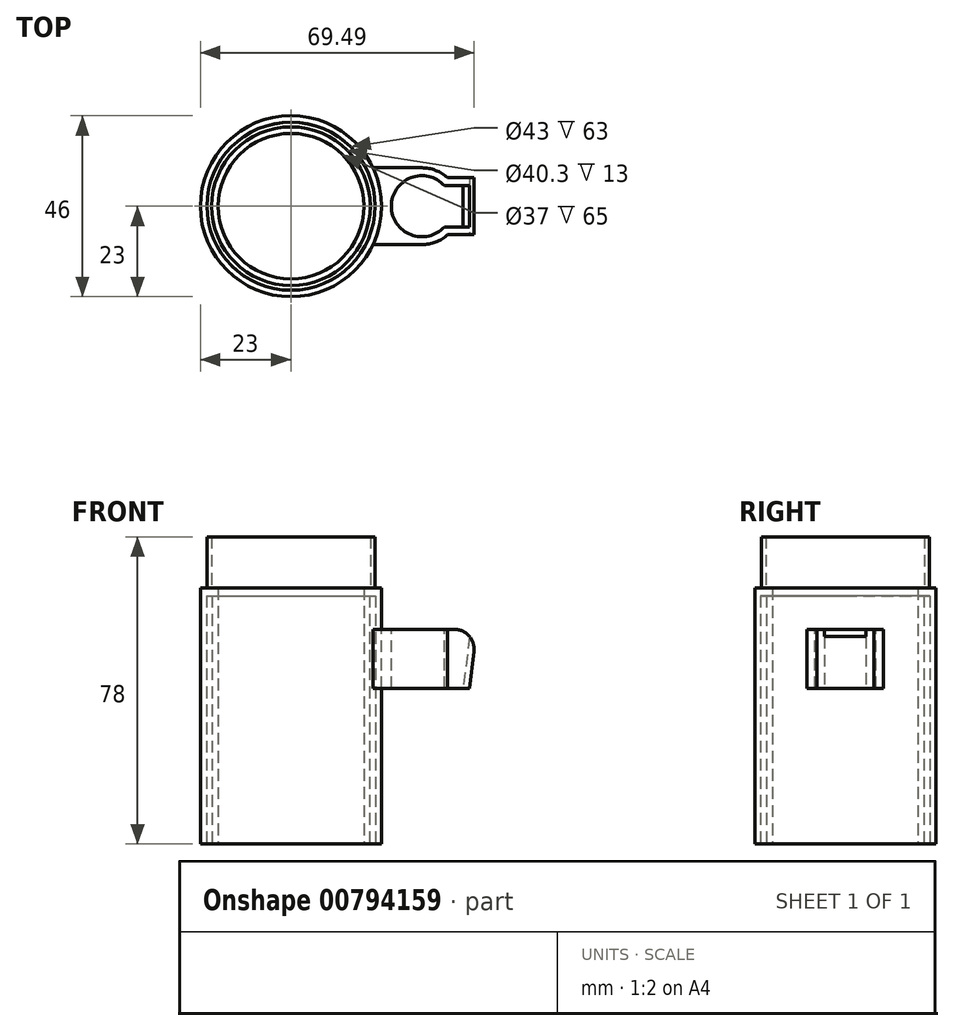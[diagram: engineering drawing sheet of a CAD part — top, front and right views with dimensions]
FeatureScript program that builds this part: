
annotation { "Feature Type Name" : "Feature", "Feature Type Description" : "" }
export const myFeature = defineFeature(function(context is Context, id is Id, definition is map)
    precondition{}
    {
        {
            var Q0;
            Q0=qCreatedBy(makeId("Front.planeOp"),FACE);
            var sketch = newSketch(context, id + "F0", { "sketchPlane" : qUnion([Q0])});
            skLineSegment(sketch, "E0.bottom", {"start": v(0, 0) * mm, "end": v(23, 0) * mm});
            skLineSegment(sketch, "E0.top", {"start": v(0, 65) * mm, "end": v(23, 65) * mm});
            skLineSegment(sketch, "E0.left", {"start": v(0, 0) * mm, "end": v(0, 65) * mm});
            skLineSegment(sketch, "E0.right", {"start": v(23, 0) * mm, "end": v(23, 65) * mm});
            skLineSegment(sketch, "E1.bottom", {"start": v(21.5, 65) * mm, "end": v(23, 65) * mm});
            skLineSegment(sketch, "E1.top", {"start": v(21.5, 0) * mm, "end": v(23, 0) * mm});
            skLineSegment(sketch, "E1.left", {"start": v(21.5, 65) * mm, "end": v(21.5, 0) * mm});
            skLineSegment(sketch, "E1.right", {"start": v(23, 65) * mm, "end": v(23, 0) * mm});
            skLineSegment(sketch, "E2.bottom", {"start": v(20, 65) * mm, "end": v(21.5, 65) * mm});
            skLineSegment(sketch, "E2.top", {"start": v(20, 0) * mm, "end": v(21.5, 0) * mm});
            skLineSegment(sketch, "E2.left", {"start": v(20, 65) * mm, "end": v(20, 0) * mm});
            skLineSegment(sketch, "E3.bottom", {"start": v(20, 65) * mm, "end": v(18.5, 65) * mm});
            skLineSegment(sketch, "E3.top", {"start": v(20, 0) * mm, "end": v(18.5, 0) * mm});
            skLineSegment(sketch, "E3.right", {"start": v(18.5, 65) * mm, "end": v(18.5, 0) * mm});
            skLineSegment(sketch, "E4.bottom", {"start": v(21.35, 65) * mm, "end": v(23, 65) * mm});
            skLineSegment(sketch, "E4.top", {"start": v(21.35, 78) * mm, "end": v(23, 78) * mm});
            skLineSegment(sketch, "E4.left", {"start": v(21.35, 65) * mm, "end": v(21.35, 78) * mm});
            skLineSegment(sketch, "E4.right", {"start": v(23, 65) * mm, "end": v(23, 78) * mm});
            skLineSegment(sketch, "E5.bottom", {"start": v(21.35, 65) * mm, "end": v(20.15, 65) * mm});
            skLineSegment(sketch, "E5.top", {"start": v(21.35, 78) * mm, "end": v(20.15, 78) * mm});
            skLineSegment(sketch, "E5.right", {"start": v(20.15, 65) * mm, "end": v(20.15, 78) * mm});
            skLineSegment(sketch, "E6.bottom", {"start": v(20.15, 78) * mm, "end": v(18.5, 78) * mm});
            skLineSegment(sketch, "E6.top", {"start": v(20.15, 65) * mm, "end": v(18.5, 65) * mm});
            skLineSegment(sketch, "E6.left", {"start": v(20.15, 78) * mm, "end": v(20.15, 65) * mm});
            skLineSegment(sketch, "E6.right", {"start": v(18.5, 78) * mm, "end": v(18.5, 65) * mm});
            skLineSegment(sketch, "E7.bottom", {"start": v(23, 65) * mm, "end": v(0, 65) * mm});
            skLineSegment(sketch, "E7.top", {"start": v(23, 63) * mm, "end": v(0, 63) * mm});
            skLineSegment(sketch, "E7.left", {"start": v(23, 65) * mm, "end": v(23, 63) * mm});
            skLineSegment(sketch, "E7.right", {"start": v(0, 65) * mm, "end": v(0, 63) * mm});
            skSolve(sketch);
        }
        {
            var Q0;
            {var subQ0=sQuery(id+"F0.wireOp",EDGE,"E3.right");var subQ1=sQuery(id+"F0.wireOp",EDGE,"E0.bottom");var subQ2=makeQuery(id+"F0.imprint","INTERSECT",VERTEX,{"derivedFrom":[subQ1,subQ0]});Q0=makeQuery(id+"F0.imprint","IMPRINT",FACE,{"disambiguationData":[TD([[makeQuery(id+"F0.imprint","IMPRINT",EDGE,{"disambiguationData":[TD([[subQ2,-1.0]])],"derivedFrom":subQ1}),1.0]])]});}
            var Q1;
            {var subQ0=sQuery(id+"F0.wireOp",EDGE,"E1.left");var subQ1=sQuery(id+"F0.wireOp",EDGE,"E0.bottom");var subQ2=makeQuery(id+"F0.imprint","INTERSECT",VERTEX,{"derivedFrom":[subQ1,subQ0]});Q1=makeQuery(id+"F0.imprint","IMPRINT",FACE,{"disambiguationData":[TD([[makeQuery(id+"F0.imprint","IMPRINT",EDGE,{"disambiguationData":[TD([[subQ2,-1.0]])],"derivedFrom":subQ1}),1.0]])]});}
            var Q2;
            {var subQ3=sQuery(id+"F0.wireOp",EDGE,"E1.left");var subQ5=sQuery(id+"F0.wireOp",EDGE,"E7.top");var subQ6=makeQuery(id+"F0.imprint","INTERSECT",VERTEX,{"derivedFrom":[subQ3,subQ5]});Q2=makeQuery(id+"F0.imprint","IMPRINT",FACE,{"disambiguationData":[TD([[makeQuery(id+"F0.imprint","IMPRINT",EDGE,{"disambiguationData":[TD([[subQ6,1.0]])],"derivedFrom":subQ3}),1.0]])]});}
            var Q3;
            {var subQ3=sQuery(id+"F0.wireOp",EDGE,"E0.top");var subQ5=makeQuery(id+"F0.imprint","INTERSECT",VERTEX,{"derivedFrom":[subQ3,sQuery(id+"F0.wireOp",EDGE,"E5.right")]});Q3=makeQuery(id+"F0.imprint","IMPRINT",FACE,{"disambiguationData":[TD([[makeQuery(id+"F0.imprint","IMPRINT",EDGE,{"disambiguationData":[TD([[subQ5,-1.0]])],"derivedFrom":subQ3}),-1.0]])]});}
            var Q4;
            {var subQ3=sQuery(id+"F0.wireOp",EDGE,"E2.left");var subQ5=sQuery(id+"F0.wireOp",EDGE,"E7.top");var subQ6=makeQuery(id+"F0.imprint","INTERSECT",VERTEX,{"derivedFrom":[subQ3,subQ5]});Q4=makeQuery(id+"F0.imprint","IMPRINT",FACE,{"disambiguationData":[TD([[makeQuery(id+"F0.imprint","IMPRINT",EDGE,{"disambiguationData":[TD([[subQ6,1.0]])],"derivedFrom":subQ3}),-1.0]])]});}
            var Q5;
            {var subQ2=sQuery(id+"F0.wireOp",EDGE,"E4.left");Q5=makeQuery(id+"F0.imprint","IMPRINT",FACE,{"disambiguationData":[TD([[makeQuery(id+"F0.imprint","IMPRINT",EDGE,{"derivedFrom":subQ2}),1.0]])]});}
            var Q6;
            Q6=sQuery(id+"F0.wireOp",EDGE,"E0.left");
            revolve(context, id + "F1", {"surfaceOperationType" : NewSurfaceOperationType.NEW, "entities" : qUnion([Q0, Q1, Q2, Q3, Q4, Q5]), "axis" : qUnion([Q6]), "revolveType" : RevolveType.FULL});
        }
        {
            var Q0;
            Q0=qCreatedBy(makeId("Front.planeOp"),FACE);
            var sketch = newSketch(context, id + "F2", { "sketchPlane" : qUnion([Q0])});
            skLineSegment(sketch, "E8", {"start": v(-23, 0) * mm, "end": v(-23, 65) * mm});
            skLineSegment(sketch, "E9", {"start": v(23, 65) * mm, "end": v(23, 0) * mm});
            skLineSegment(sketch, "E10", {"start": v(-21.35, 65) * mm, "end": v(-21.35, 78) * mm});
            skLineSegment(sketch, "E11", {"start": v(21.35, 78) * mm, "end": v(21.35, 65) * mm});
            skLineSegment(sketch, "E12.0", {"start": v(21.35, 65) * mm, "end": v(-21.35, 65) * mm});
            skLineSegment(sketch, "E13.0", {"start": v(23, 65) * mm, "end": v(-23, 65) * mm});
            skLineSegment(sketch, "E14", {"start": v(23, 54.49) * mm, "end": v(48.07, 54.49) * mm});
            skSolve(sketch);
        }
        {
            var Q0;
            Q0=sQuery(id+"F2.wireOp",EDGE,"E14");
            cPlane(context, id + "F3", {"entities" : qUnion([Q0]), "cplaneType" : CPlaneType.LINE_ANGLE, "offset" : 25 * mm, "angle" : 90 * degree, "width" : 150 * mm, "height" : 150 * mm});
        }
        {
            var Q0;
            Q0=qCreatedBy(id+"F3.planeOp",FACE);
            var sketch = newSketch(context, id + "F4", { "sketchPlane" : qUnion([Q0])});
            skCircle(sketch, "E15.0", {"center": v(0, 0) * mm, "radius": 23 * mm});
            skCircle(sketch, "E16.0", {"center": v(0, 0) * mm, "radius": 21.35 * mm});
            skPoint(sketch, "E17.middle", {"position": v(23, 0) * mm});
            skPoint(sketch, "E18", {"position": v(25.5, 0) * mm});
            skLineSegment(sketch, "E19", {"start": v(25.5, 0) * mm, "end": v(33.25, 0) * mm});
            skPoint(sketch, "E20", {"position": v(48, 0) * mm});
            skLineSegment(sketch, "E21", {"start": v(23, 0) * mm, "end": v(48, 0) * mm});
            skLineSegment(sketch, "E22", {"start": v(48, 0) * mm, "end": v(48, 5.25) * mm});
            skLineSegment(sketch, "E23", {"start": v(48, 5.25) * mm, "end": v(38.96, 5.25) * mm});
            skLineSegment(sketch, "E24.MirrorCS", {"start": v(48, -5.25) * mm, "end": v(38.96, -5.25) * mm});
            skLineSegment(sketch, "E25.MirrorCS", {"start": v(48, 0) * mm, "end": v(48, -5.25) * mm});
            skArc(sketch, "E26", {"start": v(38.96, -5.25) * mm, "mid": v(25.5, 0) * mm, "end": v(38.96, 5.25) * mm});
            skLineSegment(sketch, "E27.0", {"start": v(50, -7.25) * mm, "end": v(39.78, -7.25) * mm});
            skLineSegment(sketch, "E27.1", {"start": v(50, 0) * mm, "end": v(50, -7.25) * mm});
            skArc(sketch, "E27.2", {"start": v(39.78, -7.25) * mm, "mid": v(23.5, 0) * mm, "end": v(39.78, 7.25) * mm});
            skLineSegment(sketch, "E27.3", {"start": v(50, 7.25) * mm, "end": v(39.78, 7.25) * mm});
            skLineSegment(sketch, "E27.4", {"start": v(50, 0) * mm, "end": v(50, 7.25) * mm});
            skCircle(sketch, "E28.0", {"center": v(0, 0) * mm, "radius": 18.5 * mm});
            skLineSegment(sketch, "E29", {"start": v(33.25, 9.76) * mm, "end": v(20.83, 9.76) * mm});
            skLineSegment(sketch, "E30", {"start": v(33.25, -9.76) * mm, "end": v(20.83, -9.76) * mm});
            skSolve(sketch);
        }
        {
            var Q0;
            {var subQ0=sQuery(id+"F4.wireOp",EDGE,"E30");Q0=makeQuery(id+"F4.imprint","IMPRINT",FACE,{"disambiguationData":[TD([[makeQuery(id+"F4.imprint","IMPRINT",EDGE,{"derivedFrom":subQ0}),-1.0]])]});}
            var Q1;
            Q1=makeQuery(id+"F4.imprint","IMPRINT",FACE,{"disambiguationData":[TD([[makeQuery(id+"F4.imprint","IMPRINT",EDGE,{"derivedFrom":sQuery(id+"F4.wireOp",EDGE,"E22")}),-1.0]])]});
            var Q2;
            {var subQ0=sQuery(id+"F4.wireOp",EDGE,"E29");Q2=makeQuery(id+"F4.imprint","IMPRINT",FACE,{"disambiguationData":[TD([[makeQuery(id+"F4.imprint","IMPRINT",EDGE,{"derivedFrom":subQ0}),1.0]])]});}
            extrude(context, id + "F5", {"entities" : qUnion([Q0, Q1, Q2]), "oppositeDirection" : true, "depth" : 50 * mm, "offsetDistance" : 25 * mm, "hasSecondDirection" : true, "secondDirectionOppositeDirection" : true, "secondDirectionDepth" : -7 * mm});
        }
        {
            var Q0;
            Q0=makeQuery(id+"F5.opExtrude","SWEPT_FACE",FACE,{"disambiguationData":[OSD([sQuery(id+"F4.wireOp",EDGE,"E23")])]});
            var sketch = newSketch(context, id + "F6", { "sketchPlane" : qUnion([Q0])});
            skLineSegment(sketch, "E31.0", {"start": v(38.96, 4.49) * mm, "end": v(38.96, 61.49) * mm});
            skLineSegment(sketch, "E32.0", {"start": v(48, 61.49) * mm, "end": v(38.96, 61.49) * mm});
            skLineSegment(sketch, "E33.0", {"start": v(48, 4.49) * mm, "end": v(48, 61.49) * mm});
            skLineSegment(sketch, "E34.0", {"start": v(48, 4.49) * mm, "end": v(38.96, 4.49) * mm});
            skLineSegment(sketch, "E35", {"start": v(46.46, 61.49) * mm, "end": v(39.46, 4.49) * mm});
            skLineSegment(sketch, "E36", {"start": v(48, 61.49) * mm, "end": v(41, 4.49) * mm});
            skLineSegment(sketch, "E37.0", {"start": v(50, 61.49) * mm, "end": v(39.78, 61.49) * mm});
            skLineSegment(sketch, "E38.0", {"start": v(50, 4.49) * mm, "end": v(50, 61.49) * mm});
            skLineSegment(sketch, "E39.0", {"start": v(50, 4.49) * mm, "end": v(39.78, 4.49) * mm});
            skSolve(sketch);
        }
        {
            var Q0;
            {var subQ0=sQuery(id+"F6.wireOp",EDGE,"E33.0");Q0=makeQuery(id+"F6.imprint","IMPRINT",FACE,{"disambiguationData":[TD([[makeQuery(id+"F6.imprint","IMPRINT",EDGE,{"derivedFrom":subQ0}),1.0]])]});}
            var Q1;
            {var subQ1=sQuery(id+"F6.wireOp",EDGE,"E35");Q1=makeQuery(id+"F6.imprint","IMPRINT",FACE,{"disambiguationData":[TD([[makeQuery(id+"F6.imprint","IMPRINT",EDGE,{"derivedFrom":subQ1}),1.0]])]});}
            extrude(context, id + "F7", {"entities" : qUnion([Q0, Q1]), "operationType" : NewBodyOperationType.ADD, "depth" : 10.7 * mm, "offsetDistance" : 25 * mm});
        }
        {
            var Q0;
            {var subQ0=sQuery(id+"F6.wireOp",EDGE,"E33.0");Q0=makeQuery(id+"F6.imprint","IMPRINT",FACE,{"disambiguationData":[TD([[makeQuery(id+"F6.imprint","IMPRINT",EDGE,{"derivedFrom":subQ0}),-1.0]])]});}
            var Q1;
            {var subQ0=sQuery(id+"F6.wireOp",EDGE,"E33.0");Q1=makeQuery(id+"F6.imprint","IMPRINT",FACE,{"disambiguationData":[TD([[makeQuery(id+"F6.imprint","IMPRINT",EDGE,{"derivedFrom":subQ0}),1.0]])]});}
            extrude(context, id + "F8", {"entities" : qUnion([Q0, Q1]), "operationType" : NewBodyOperationType.REMOVE, "depth" : 25 * mm, "offsetDistance" : 25 * mm, "symmetric" : true});
        }
        {
            var Q0;
            {var subQ1=sQuery(id+"F4.wireOp",EDGE,"E19");Q0=makeQuery(id+"F4.imprint","IMPRINT",FACE,{"disambiguationData":[TD([[makeQuery(id+"F4.imprint","IMPRINT",EDGE,{"derivedFrom":subQ1}),-1.0]])]});}
            var Q1;
            {var subQ2=sQuery(id+"F4.wireOp",EDGE,"E19");Q1=makeQuery(id+"F4.imprint","IMPRINT",FACE,{"disambiguationData":[TD([[makeQuery(id+"F4.imprint","IMPRINT",EDGE,{"derivedFrom":subQ2}),1.0]])]});}
            var Q2;
            Q2=makeQuery(id+"F4.imprint","IMPRINT",FACE,{"disambiguationData":[TD([[makeQuery(id+"F4.imprint","IMPRINT",EDGE,{"derivedFrom":sQuery(id+"F4.wireOp",EDGE,"E22")}),-1.0]])]});
            var Q3;
            {var subQ0=sQuery(id+"F4.wireOp",EDGE,"E30");Q3=makeQuery(id+"F4.imprint","IMPRINT",FACE,{"disambiguationData":[TD([[makeQuery(id+"F4.imprint","IMPRINT",EDGE,{"derivedFrom":subQ0}),-1.0]])]});}
            var Q4;
            {var subQ0=sQuery(id+"F4.wireOp",EDGE,"E29");Q4=makeQuery(id+"F4.imprint","IMPRINT",FACE,{"disambiguationData":[TD([[makeQuery(id+"F4.imprint","IMPRINT",EDGE,{"derivedFrom":subQ0}),1.0]])]});}
            extrude(context, id + "F9", {"entities" : qUnion([Q0, Q1, Q2, Q3, Q4]), "operationType" : NewBodyOperationType.REMOVE, "oppositeDirection" : true, "depth" : 0 * mm, "offsetDistance" : 25 * mm, "hasSecondDirection" : true, "secondDirectionOppositeDirection" : false, "secondDirectionDepth" : 7 * mm});
        }
        {
            var Q0;
            {var subQ1=sQuery(id+"F4.wireOp",EDGE,"E19");Q0=makeQuery(id+"F4.imprint","IMPRINT",FACE,{"disambiguationData":[TD([[makeQuery(id+"F4.imprint","IMPRINT",EDGE,{"derivedFrom":subQ1}),-1.0]])]});}
            var Q1;
            Q1=makeQuery(id+"F4.imprint","IMPRINT",FACE,{"disambiguationData":[TD([[makeQuery(id+"F4.imprint","IMPRINT",EDGE,{"derivedFrom":sQuery(id+"F4.wireOp",EDGE,"E22")}),-1.0]])]});
            var Q2;
            {var subQ0=sQuery(id+"F4.wireOp",EDGE,"E30");Q2=makeQuery(id+"F4.imprint","IMPRINT",FACE,{"disambiguationData":[TD([[makeQuery(id+"F4.imprint","IMPRINT",EDGE,{"derivedFrom":subQ0}),-1.0]])]});}
            var Q3;
            {var subQ2=sQuery(id+"F4.wireOp",EDGE,"E19");Q3=makeQuery(id+"F4.imprint","IMPRINT",FACE,{"disambiguationData":[TD([[makeQuery(id+"F4.imprint","IMPRINT",EDGE,{"derivedFrom":subQ2}),1.0]])]});}
            var Q4;
            {var subQ0=sQuery(id+"F4.wireOp",EDGE,"E29");Q4=makeQuery(id+"F4.imprint","IMPRINT",FACE,{"disambiguationData":[TD([[makeQuery(id+"F4.imprint","IMPRINT",EDGE,{"derivedFrom":subQ0}),1.0]])]});}
            extrude(context, id + "F10", {"entities" : qUnion([Q0, Q1, Q2, Q3, Q4]), "operationType" : NewBodyOperationType.REMOVE, "oppositeDirection" : true, "depth" : 62 * mm, "offsetDistance" : 25 * mm, "hasSecondDirection" : true, "secondDirectionOppositeDirection" : false, "secondDirectionDepth" : -15 * mm});
        }
        {
            var Q0;
            Q0=makeQuery(id+"F9.boolean.opBoolean","COPY",EDGE,{"derivedFrom":makeQuery(id+"F9.opExtrude","CAP_EDGE",EDGE,{"disambiguationData":[OSD([sQuery(id+"F4.wireOp",EDGE,"E29")])],"isStart":false})});
            var Q1;
            Q1=makeQuery(id+"F9.boolean.opBoolean","COPY",EDGE,{"derivedFrom":makeQuery(id+"F9.opExtrude","CAP_EDGE",EDGE,{"disambiguationData":[OSD([sQuery(id+"F4.wireOp",EDGE,"E27.3")])],"isStart":false})});
            var Q2;
            Q2=makeQuery(id+"F9.boolean.opBoolean","COPY",EDGE,{"derivedFrom":makeQuery(id+"F9.opExtrude","CAP_EDGE",EDGE,{"disambiguationData":[OSD([sQuery(id+"F4.wireOp",EDGE,"E30")])],"isStart":false})});
            var Q3;
            Q3=makeQuery(id+"F9.boolean.opBoolean","COPY",EDGE,{"derivedFrom":makeQuery(id+"F9.opExtrude","CAP_EDGE",EDGE,{"disambiguationData":[OSD([sQuery(id+"F4.wireOp",EDGE,"E27.0")])],"isStart":false})});
            var Q4;
            Q4=makeQuery(id+"F9.boolean.opBoolean","INTERSECT",EDGE,{"derivedFrom":[makeQuery(id+"F8.boolean.opBoolean","COPY",FACE,{"derivedFrom":makeQuery(id+"F8.opExtrude","SWEPT_FACE",FACE,{"disambiguationData":[OSD([sQuery(id+"F6.wireOp",EDGE,"E36")])]})}),makeQuery(id+"F9.opExtrude","CAP_FACE",FACE,{"disambiguationData":[OSD([sQuery(id+"F4.wireOp",EDGE,"E15.0"),sQuery(id+"F4.wireOp",EDGE,"E27.0"),sQuery(id+"F4.wireOp",EDGE,"E27.1"),sQuery(id+"F4.wireOp",EDGE,"E27.2"),sQuery(id+"F4.wireOp",EDGE,"E27.3"),sQuery(id+"F4.wireOp",EDGE,"E27.4"),sQuery(id+"F4.wireOp",EDGE,"E29"),sQuery(id+"F4.wireOp",EDGE,"E30")])],"isStart":false})]});
            fillet(context, id + "F11", {"entities" : qUnion([Q0, Q1, Q2, Q3, Q4]), "radius" : 5 * mm, "tangentPropagation" : true, "allowEdgeOverflow" : false});
        }
    });
